# Revit family: SD1010BR_SD1010PTO
name_source: partatom
category: Luminárias
units: mm (PartAtom-declared; Revit-internal decimal feet)

## family parameters
Compartilhado = Não
Corte com vazios quando carregada = Não
Cota do conector redondo = Utilizar diâmetro
Fonte luminosa = Não
Hospedeiro = Forro
Manter orientação da anotação = Não
Número OmniClass = 23.80.70.11
Ponto de cálculo do ambiente = Não
Sempre na vertical = Sim
Tipo de parte = Normal
Título OmniClass = Luminaries for Internal Lighting

## types (2) — shared parameters
Altura = 0.02 m
Comprimento = 1 m
Fabricante = Stella
Grau de proteção (IP) = IP20
Largura = 0.04 m
Modelo = Trilho ECO de Sobrepor

Trilho ECO de Sobrepor
Trace - Trilho de Sobrepor 1m
Potência máxima = 1000 W
Tensão Elétrica = 127V-220V
URL = https://stella.com.br
zero-valued in all types: Elevação padrão

## per-type parameters (varying)
| type | Estrutura | Referência |
| SD1010BR - BRANCO - 1m | Al - Branco | SD1010BR |
| SD1010PTO - PRETO - 1m | Al - Preto | SD1010PTO |
